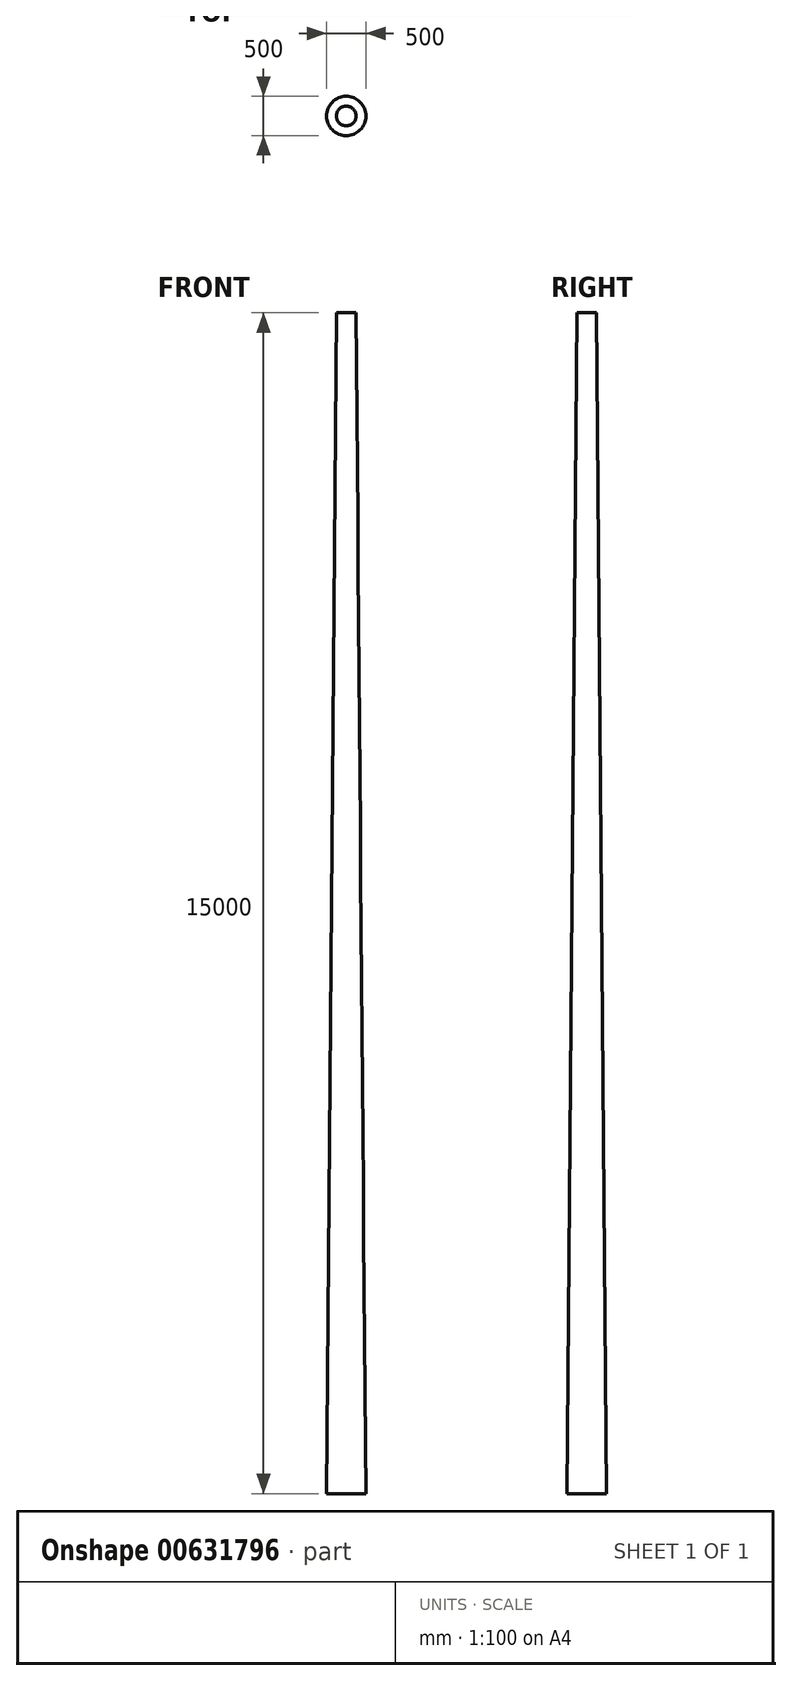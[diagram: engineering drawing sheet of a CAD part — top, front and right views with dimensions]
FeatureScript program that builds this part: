
annotation { "Feature Type Name" : "Feature", "Feature Type Description" : "" }
export const myFeature = defineFeature(function(context is Context, id is Id, definition is map)
    precondition{}
    {
        {
            var Q0;
            Q0=qCreatedBy(makeId("Top.planeOp"),FACE);
            var sketch = newSketch(context, id + "F0", { "sketchPlane" : qUnion([Q0])});
            skCircle(sketch, "E0", {"center": v(0, 0) * mm, "radius": 250 * mm});
            skSolve(sketch);
        }
        {
            var Q0;
            Q0=qCreatedBy(makeId("Top.planeOp"),FACE);
            cPlane(context, id + "F1", {"entities" : qUnion([Q0]), "cplaneType" : CPlaneType.OFFSET, "offset" : 15000 * mm, "width" : 150 * mm, "height" : 150 * mm});
        }
        {
            var Q0;
            Q0=qCreatedBy(id+"F1.planeOp",FACE);
            var sketch = newSketch(context, id + "F2", { "sketchPlane" : qUnion([Q0])});
            skCircle(sketch, "E1", {"center": v(0, 0) * mm, "radius": 125 * mm});
            skSolve(sketch);
        }
        {
            var Q0;
            Q0 = qSketchRegion(id + "F0", true);
            var Q1;
            Q1 = qSketchRegion(id + "F2", true);
            loft(context, id + "F3", {"sheetProfilesArray" : [{ "sheetProfileEntities" : qUnion([Q0]) }, { "sheetProfileEntities" : qUnion([Q1]) }]});
        }
    });
